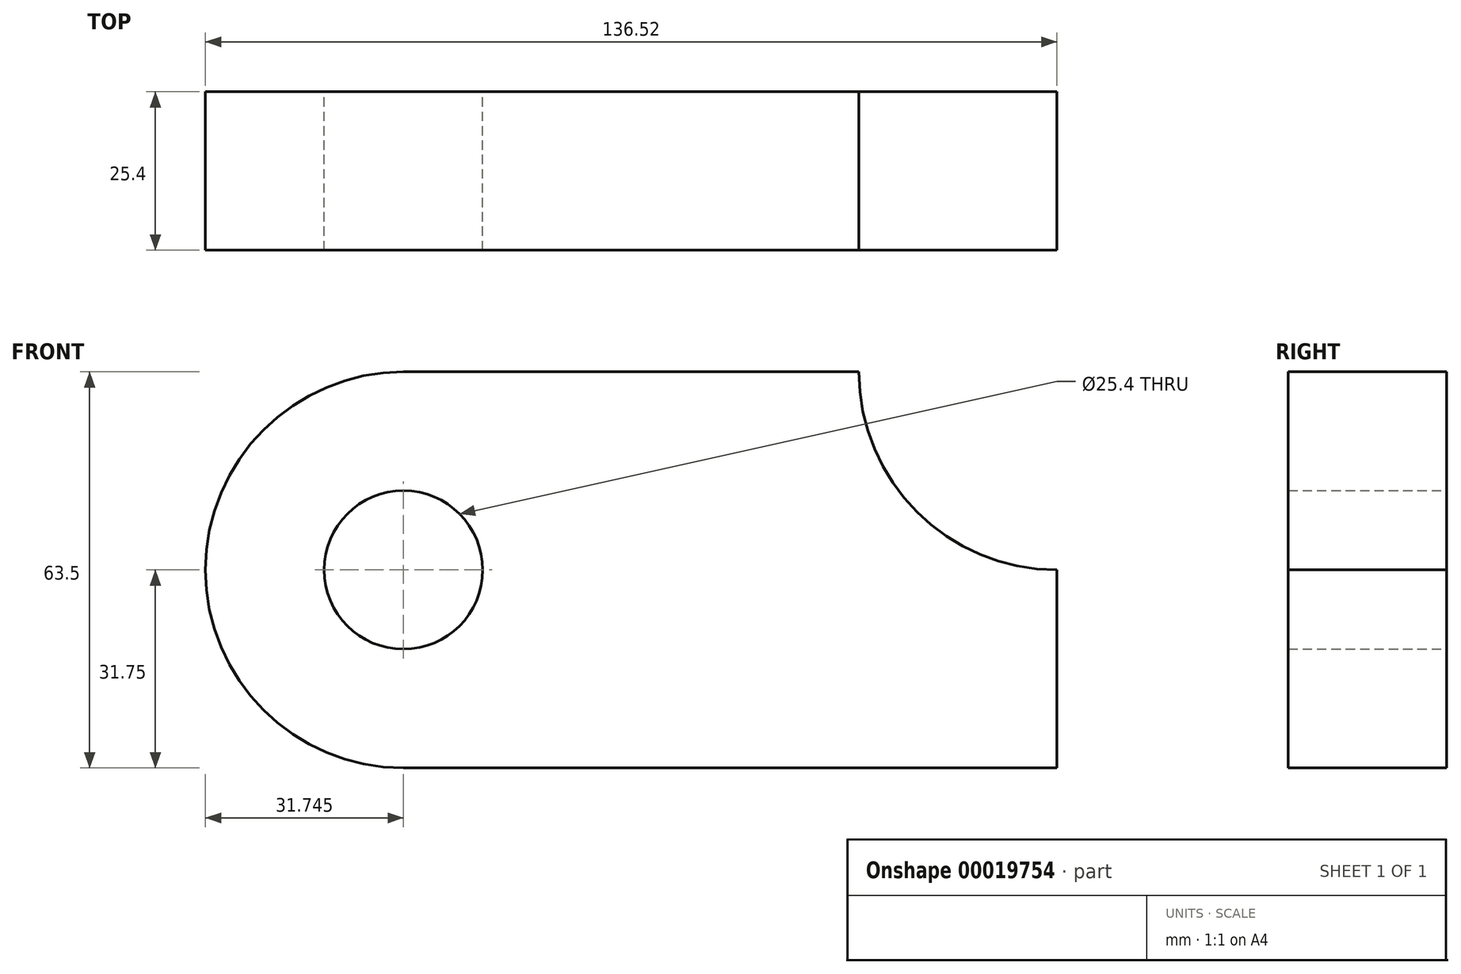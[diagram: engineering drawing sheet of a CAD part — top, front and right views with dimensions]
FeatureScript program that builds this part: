
annotation { "Feature Type Name" : "Feature", "Feature Type Description" : "" }
export const myFeature = defineFeature(function(context is Context, id is Id, definition is map)
    precondition{}
    {
        {
            var Q0;
            Q0=qCreatedBy(makeId("Front.planeOp"),FACE);
            var sketch = newSketch(context, id + "F0", { "sketchPlane" : qUnion([Q0])});
            skLineSegment(sketch, "E0.bottom", {"start": v(0, 0) * mm, "end": v(-104.77, 0) * mm});
            skLineSegment(sketch, "E0.top", {"start": v(-31.75, 63.5) * mm, "end": v(-104.78, 63.5) * mm});
            skLineSegment(sketch, "E0.left", {"start": v(0, 0) * mm, "end": v(0, 31.75) * mm});
            skArc(sketch, "E1", {"start": v(-31.75, 63.5) * mm, "mid": v(-22.45, 41.05) * mm, "end": v(0, 31.75) * mm});
            skArc(sketch, "E2", {"start": v(-104.78, 63.5) * mm, "mid": v(-136.53, 31.75) * mm, "end": v(-104.77, 0) * mm});
            skCircle(sketch, "E3", {"center": v(-104.77, 31.75) * mm, "radius": 12.7 * mm});
            skSolve(sketch);
        }
        {
            var Q0;
            Q0=makeQuery(id+"F0.imprint","IMPRINT",FACE,{"disambiguationData":[TD([[makeQuery(id+"F0.imprint","IMPRINT",EDGE,{"derivedFrom":sQuery(id+"F0.wireOp",EDGE,"E0.bottom")}),-1.0]])]});
            extrude(context, id + "F1", {"entities" : qUnion([Q0]), "depth" : 25.4 * mm});
        }
    });
